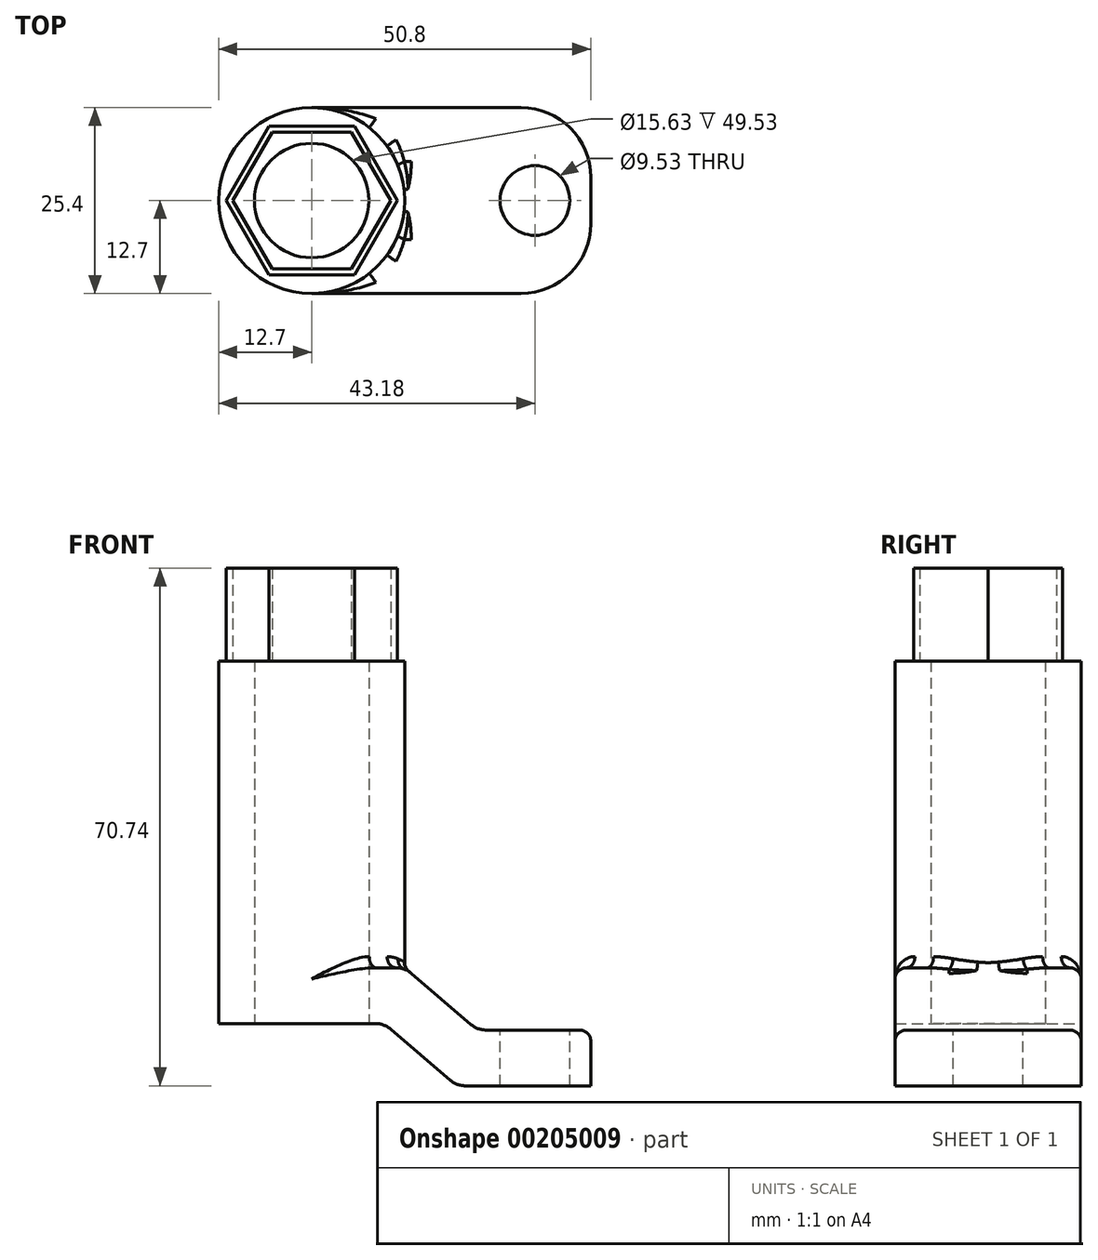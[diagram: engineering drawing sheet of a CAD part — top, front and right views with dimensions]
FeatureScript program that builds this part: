
annotation { "Feature Type Name" : "Feature", "Feature Type Description" : "" }
export const myFeature = defineFeature(function(context is Context, id is Id, definition is map)
    precondition{}
    {
        {
            var Q0;
            Q0=qCreatedBy(makeId("Front.planeOp"),FACE);
            var sketch = newSketch(context, id + "F0", { "sketchPlane" : qUnion([Q0])});
            skLineSegment(sketch, "E0", {"start": v(38.1, 0) * mm, "end": v(19.82, 0) * mm});
            skLineSegment(sketch, "E1", {"start": v(19.82, 0) * mm, "end": v(9.88, 8.5) * mm});
            skLineSegment(sketch, "E2", {"start": v(9.88, 8.5) * mm, "end": v(-12.7, 8.5) * mm});
            skLineSegment(sketch, "E3", {"start": v(-12.7, 8.5) * mm, "end": v(-12.7, 16.13) * mm});
            skLineSegment(sketch, "E4", {"start": v(38.1, 7.62) * mm, "end": v(38.1, 0) * mm});
            skLineSegment(sketch, "E5", {"start": v(-12.7, 16.13) * mm, "end": v(12.7, 16.13) * mm});
            skLineSegment(sketch, "E6", {"start": v(12.7, 16.13) * mm, "end": v(22.64, 7.62) * mm});
            skLineSegment(sketch, "E7", {"start": v(0, 0) * mm, "end": v(0, 16.13) * mm, "construction": true});
            skLineSegment(sketch, "E8", {"start": v(38.1, 7.62) * mm, "end": v(21.59, 7.62) * mm});
            skPoint(sketch, "E9.orphan", {"position": v(38.1, 8.04) * mm});
            skPoint(sketch, "E10.orphan", {"position": v(21.6, 8.5) * mm});
            skSolve(sketch);
        }
        {
            var Q0;
            Q0=makeQuery(id+"F0.imprint","IMPRINT",FACE,{"disambiguationData":[TD([[makeQuery(id+"F0.imprint","IMPRINT",EDGE,{"derivedFrom":sQuery(id+"F0.wireOp",EDGE,"E0")}),-1.0]])]});
            extrude(context, id + "F1", {"entities" : qUnion([Q0]), "endBound" : BoundingType.SYMMETRIC, "depth" : 25.4 * mm});
        }
        {
            var Q0;
            Q0=makeQuery(id+"F1.opExtrude","SWEPT_FACE",FACE,{"disambiguationData":[OSD([sQuery(id+"F0.wireOp",EDGE,"E5")])]});
            var sketch = newSketch(context, id + "F2", { "sketchPlane" : qUnion([Q0])});
            skCircle(sketch, "E11", {"center": v(0, 0) * mm, "radius": 7.82 * mm});
            skCircle(sketch, "E12", {"center": v(0, 0) * mm, "radius": 12.7 * mm});
            skSolve(sketch);
        }
        {
            var Q0;
            Q0=makeQuery(id+"F2.imprint","IMPRINT",FACE,{"disambiguationData":[TD([[makeQuery(id+"F2.imprint","IMPRINT",EDGE,{"derivedFrom":sQuery(id+"F2.wireOp",EDGE,"E11")}),-1.0]])]});
            extrude(context, id + "F3", {"entities" : qUnion([Q0]), "operationType" : NewBodyOperationType.ADD, "depth" : 41.9 * mm});
        }
        {
            var Q0;
            Q0=makeQuery(id+"F3.opExtrude","CAP_FACE",FACE,{"disambiguationData":[OSD([sQuery(id+"F2.wireOp",EDGE,"E11"),sQuery(id+"F2.wireOp",EDGE,"E12")])],"isStart":false});
            var sketch = newSketch(context, id + "F4", { "sketchPlane" : qUnion([Q0])});
            skCircle(sketch, "E13.cCircle", {"center": v(0, 0) * mm, "radius": 9.34 * mm, "construction": true});
            skLineSegment(sketch, "E13.0", {"start": v(5.4, 9.34) * mm, "end": v(10.79, 0) * mm});
            skLineSegment(sketch, "E13.1", {"start": v(10.79, 0) * mm, "end": v(5.4, -9.34) * mm});
            skLineSegment(sketch, "E13.2", {"start": v(5.4, -9.34) * mm, "end": v(-5.4, -9.34) * mm});
            skLineSegment(sketch, "E13.3", {"start": v(-5.4, -9.34) * mm, "end": v(-10.79, 0) * mm});
            skLineSegment(sketch, "E13.4", {"start": v(-10.79, 0) * mm, "end": v(-5.4, 9.34) * mm});
            skLineSegment(sketch, "E13.5", {"start": v(-5.4, 9.34) * mm, "end": v(5.4, 9.34) * mm});
            skPoint(sketch, "E13.0.midPoint", {"position": v(8.09, 4.67) * mm});
            skLineSegment(sketch, "E14", {"start": v(0, 0) * mm, "end": v(0, 9.34) * mm});
            skCircle(sketch, "E15.cCircle", {"center": v(0, 0) * mm, "radius": 10.14 * mm, "construction": true});
            skLineSegment(sketch, "E15.0", {"start": v(-5.85, 10.14) * mm, "end": v(5.85, 10.14) * mm});
            skLineSegment(sketch, "E15.1", {"start": v(5.85, 10.14) * mm, "end": v(11.7, 0) * mm});
            skLineSegment(sketch, "E15.2", {"start": v(11.7, 0) * mm, "end": v(5.85, -10.14) * mm});
            skLineSegment(sketch, "E15.3", {"start": v(5.85, -10.14) * mm, "end": v(-5.85, -10.14) * mm});
            skLineSegment(sketch, "E15.4", {"start": v(-5.85, -10.14) * mm, "end": v(-11.7, 0) * mm});
            skLineSegment(sketch, "E15.5", {"start": v(-11.7, 0) * mm, "end": v(-5.85, 10.14) * mm});
            skPoint(sketch, "E15.0.midPoint", {"position": v(0, 10.14) * mm});
            skSolve(sketch);
        }
        {
            var Q0;
            {var subQ0=sQuery(id+"F2.wireOp",EDGE,"E11");Q0=makeQuery(id+"F6.boolean.opBoolean","SPLIT",FACE,{"disambiguationData":[TD([makeQuery(id+"F3.opExtrude","SWEPT_FACE",FACE,{"disambiguationData":[OSD([subQ0])]})])],"derivedFrom":makeQuery(id+"F3.opExtrude","CAP_FACE",FACE,{"disambiguationData":[OSD([subQ0,sQuery(id+"F2.wireOp",EDGE,"E12")])],"isStart":false})});}
            var sketch = newSketch(context, id + "F5", { "sketchPlane" : qUnion([Q0])});
            skCircle(sketch, "E16.cCircle", {"center": v(0, 0) * mm, "radius": 10.26 * mm, "construction": true});
            skLineSegment(sketch, "E16.0", {"start": v(-5.92, 10.26) * mm, "end": v(5.92, 10.26) * mm});
            skLineSegment(sketch, "E16.1", {"start": v(5.92, 10.26) * mm, "end": v(11.85, 0) * mm});
            skLineSegment(sketch, "E16.2", {"start": v(11.85, 0) * mm, "end": v(5.92, -10.26) * mm});
            skLineSegment(sketch, "E16.3", {"start": v(5.92, -10.26) * mm, "end": v(-5.92, -10.26) * mm});
            skLineSegment(sketch, "E16.4", {"start": v(-5.92, -10.26) * mm, "end": v(-11.85, 0) * mm});
            skLineSegment(sketch, "E16.5", {"start": v(-11.85, 0) * mm, "end": v(-5.92, 10.26) * mm});
            skPoint(sketch, "E16.0.midPoint", {"position": v(0, 10.26) * mm});
            skCircle(sketch, "E17.cCircle", {"center": v(0, 0) * mm, "radius": 9.21 * mm, "construction": true});
            skLineSegment(sketch, "E17.0", {"start": v(-5.32, 9.21) * mm, "end": v(5.32, 9.21) * mm});
            skLineSegment(sketch, "E17.1", {"start": v(5.32, 9.21) * mm, "end": v(10.64, 0) * mm});
            skLineSegment(sketch, "E17.2", {"start": v(10.64, 0) * mm, "end": v(5.32, -9.21) * mm});
            skLineSegment(sketch, "E17.3", {"start": v(5.32, -9.21) * mm, "end": v(-5.32, -9.21) * mm});
            skLineSegment(sketch, "E17.4", {"start": v(-5.32, -9.21) * mm, "end": v(-10.64, 0) * mm});
            skLineSegment(sketch, "E17.5", {"start": v(-10.64, 0) * mm, "end": v(-5.32, 9.21) * mm});
            skPoint(sketch, "E17.0.midPoint", {"position": v(0, 9.21) * mm});
            skSolve(sketch);
        }
        {
            var Q0;
            {var subQ3=sQuery(id+"F4.wireOp",EDGE,"E13.0");Q0=makeQuery(id+"F4.imprint","IMPRINT",FACE,{"disambiguationData":[TD([[makeQuery(id+"F4.imprint","IMPRINT",EDGE,{"derivedFrom":subQ3}),1.0]])]});}
            extrude(context, id + "F6", {"entities" : qUnion([Q0]), "operationType" : NewBodyOperationType.ADD, "depth" : 12.7 * mm});
        }
        {
            var Q0;
            {var subQ0=sQuery(id+"F0.wireOp",EDGE,"E5");var subQ1=sQuery(id+"F0.wireOp",EDGE,"E3");var subQ2=makeQuery(id+"F1.opExtrude","SWEPT_FACE",FACE,{"disambiguationData":[OSD([subQ0])]});Q0=makeQuery(id+"F3.boolean.opBoolean","SPLIT",FACE,{"disambiguationData":[TD([makeQuery(id+"F1.opExtrude","CAP_FACE",FACE,{"disambiguationData":[OSD([sQuery(id+"F0.wireOp",EDGE,"E0"),sQuery(id+"F0.wireOp",EDGE,"E1"),sQuery(id+"F0.wireOp",EDGE,"E2"),subQ1,sQuery(id+"F0.wireOp",EDGE,"wxQY32r5-ra9H-VeKz-igtE-eNKNYk2lJN9U"),sQuery(id+"F0.wireOp",EDGE,"E4"),subQ0,sQuery(id+"F0.wireOp",EDGE,"E6")])],"isStart":true}),makeQuery(id+"F1.opExtrude","SWEPT_FACE",FACE,{"disambiguationData":[OSD([subQ1])]}),subQ2,makeQuery(id+"F3.opExtrude","SWEPT_FACE",FACE,{"disambiguationData":[OSD([sQuery(id+"F2.wireOp",EDGE,"E12")])]})])],"derivedFrom":subQ2});}
            var Q1;
            {var subQ0=sQuery(id+"F0.wireOp",EDGE,"E5");var subQ1=sQuery(id+"F0.wireOp",EDGE,"E3");var subQ2=makeQuery(id+"F1.opExtrude","SWEPT_FACE",FACE,{"disambiguationData":[OSD([subQ0])]});Q1=makeQuery(id+"F3.boolean.opBoolean","SPLIT",FACE,{"disambiguationData":[TD([makeQuery(id+"F1.opExtrude","CAP_FACE",FACE,{"disambiguationData":[OSD([sQuery(id+"F0.wireOp",EDGE,"E0"),sQuery(id+"F0.wireOp",EDGE,"E1"),sQuery(id+"F0.wireOp",EDGE,"E2"),subQ1,sQuery(id+"F0.wireOp",EDGE,"wxQY32r5-ra9H-VeKz-igtE-eNKNYk2lJN9U"),sQuery(id+"F0.wireOp",EDGE,"E4"),subQ0,sQuery(id+"F0.wireOp",EDGE,"E6")])],"isStart":false}),makeQuery(id+"F1.opExtrude","SWEPT_FACE",FACE,{"disambiguationData":[OSD([subQ1])]}),subQ2,makeQuery(id+"F3.opExtrude","SWEPT_FACE",FACE,{"disambiguationData":[OSD([sQuery(id+"F2.wireOp",EDGE,"E12")])]})])],"derivedFrom":subQ2});}
            var Q2;
            Q2=makeQuery(id+"F3.boolean.opBoolean","SPLIT",FACE,{"disambiguationData":[TD([makeQuery(id+"F3.opExtrude","SWEPT_FACE",FACE,{"disambiguationData":[OSD([sQuery(id+"F2.wireOp",EDGE,"E11")])]})])],"derivedFrom":makeQuery(id+"F1.opExtrude","SWEPT_FACE",FACE,{"disambiguationData":[OSD([sQuery(id+"F0.wireOp",EDGE,"E5")])]})});
            extrude(context, id + "F7", {"entities" : qUnion([Q0, Q1, Q2]), "operationType" : NewBodyOperationType.REMOVE, "endBound" : BoundingType.THROUGH_ALL, "oppositeDirection" : true, "depth" : 25.4 * mm});
        }
        {
            var Q0;
            Q0=makeQuery(id+"F1.opExtrude","SWEPT_FACE",FACE,{"disambiguationData":[OSD([sQuery(id+"F0.wireOp",EDGE,"E8")])]});
            var sketch = newSketch(context, id + "F8", { "sketchPlane" : qUnion([Q0])});
            skCircle(sketch, "E18", {"center": v(30.48, 0) * mm, "radius": 4.76 * mm});
            skSolve(sketch);
        }
        {
            var Q0;
            Q0=makeQuery(id+"F8.imprint","IMPRINT",FACE,{"disambiguationData":[TD([[makeQuery(id+"F8.imprint","IMPRINT",EDGE,{"derivedFrom":sQuery(id+"F8.wireOp",EDGE,"E18")}),1.0]])]});
            extrude(context, id + "F9", {"entities" : qUnion([Q0]), "operationType" : NewBodyOperationType.REMOVE, "endBound" : BoundingType.THROUGH_ALL, "oppositeDirection" : true, "depth" : 25.4 * mm});
        }
        {
            var Q0;
            Q0=makeQuery(id+"F1.opExtrude","CAP_EDGE",EDGE,{"disambiguationData":[OSD([sQuery(id+"F0.wireOp",EDGE,"E4")])],"isStart":true});
            var Q1;
            Q1=makeQuery(id+"F1.opExtrude","CAP_EDGE",EDGE,{"disambiguationData":[OSD([sQuery(id+"F0.wireOp",EDGE,"E4")])],"isStart":false});
            fillet(context, id + "F10", {"entities" : qUnion([Q0, Q1]), "radius" : 9.52 * mm, "tangentPropagation" : true, "allowEdgeOverflow" : false});
        }
        {
            var Q0;
            Q0=makeQuery(id+"F1.opExtrude","SWEPT_EDGE",EDGE,{"disambiguationData":[OSD([sQuery(id+"F0.wireOp",EDGE,"wxQY32r5-ra9H-VeKz-igtE-eNKNYk2lJN9U"),sQuery(id+"F0.wireOp",EDGE,"E6")])]});
            var Q1;
            Q1=makeQuery(id+"F1.opExtrude","SWEPT_EDGE",EDGE,{"disambiguationData":[OSD([sQuery(id+"F0.wireOp",EDGE,"E0"),sQuery(id+"F0.wireOp",EDGE,"E1")])]});
            var Q2;
            Q2=makeQuery(id+"F1.opExtrude","SWEPT_EDGE",EDGE,{"disambiguationData":[OSD([sQuery(id+"F0.wireOp",EDGE,"E1"),sQuery(id+"F0.wireOp",EDGE,"E2")])]});
            fillet(context, id + "F11", {"entities" : qUnion([Q0, Q1, Q2]), "radius" : 3.17 * mm, "tangentPropagation" : true, "allowEdgeOverflow" : false});
        }
        {
            var Q0;
            {var subQ0=sQuery(id+"F0.wireOp",EDGE,"E6");var subQ1=sQuery(id+"F0.wireOp",EDGE,"E5");var subQ2=sQuery(id+"F2.wireOp",EDGE,"E12");Q0=makeQuery(id+"F3.boolean.opBoolean","SPLIT",EDGE,{"disambiguationData":[TD([makeQuery(id+"F1.opExtrude","CAP_FACE",FACE,{"disambiguationData":[OSD([sQuery(id+"F0.wireOp",EDGE,"E0"),sQuery(id+"F0.wireOp",EDGE,"E1"),sQuery(id+"F0.wireOp",EDGE,"E2"),sQuery(id+"F0.wireOp",EDGE,"E3"),sQuery(id+"F0.wireOp",EDGE,"wxQY32r5-ra9H-VeKz-igtE-eNKNYk2lJN9U"),sQuery(id+"F0.wireOp",EDGE,"E4"),subQ1,subQ0])],"isStart":false}),makeQuery(id+"F1.opExtrude","SWEPT_FACE",FACE,{"disambiguationData":[OSD([subQ1])]}),makeQuery(id+"F1.opExtrude","SWEPT_FACE",FACE,{"disambiguationData":[OSD([subQ0])]}),makeQuery(id+"F3.opExtrude","SWEPT_FACE",FACE,{"disambiguationData":[OSD([subQ2])]})])],"derivedFrom":makeQuery(id+"F3.opExtrude","CAP_EDGE",EDGE,{"disambiguationData":[OSD([subQ2])],"isStart":true})});}
            var Q1;
            {var subQ0=sQuery(id+"F0.wireOp",EDGE,"E6");var subQ1=sQuery(id+"F0.wireOp",EDGE,"E5");Q1=makeQuery(id+"F3.boolean.opBoolean","SPLIT",EDGE,{"disambiguationData":[TD([makeQuery(id+"F1.opExtrude","SWEPT_FACE",FACE,{"disambiguationData":[OSD([subQ0])]})])],"derivedFrom":makeQuery(id+"F1.opExtrude","CAP_EDGE",EDGE,{"disambiguationData":[OSD([subQ1])],"isStart":false})});}
            var Q2;
            Q2=makeQuery(id+"F1.opExtrude","CAP_EDGE",EDGE,{"disambiguationData":[OSD([sQuery(id+"F0.wireOp",EDGE,"E6")])],"isStart":false});
            var Q3;
            {var subQ0=sQuery(id+"F0.wireOp",EDGE,"E6");var subQ1=sQuery(id+"F0.wireOp",EDGE,"E5");Q3=makeQuery(id+"F3.boolean.opBoolean","SPLIT",EDGE,{"disambiguationData":[TD([makeQuery(id+"F1.opExtrude","SWEPT_FACE",FACE,{"disambiguationData":[OSD([subQ0])]})])],"derivedFrom":makeQuery(id+"F1.opExtrude","CAP_EDGE",EDGE,{"disambiguationData":[OSD([subQ1])],"isStart":true})});}
            fillet(context, id + "F12", {"entities" : qUnion([Q0, Q1, Q2, Q3]), "radius" : 1.52 * mm, "tangentPropagation" : true, "allowEdgeOverflow" : false});
        }
    });
